# Revit family: xxxSoap_Dispenser-Grohe-Universal-40553_Series
name_source: partatom
category: Specialty Equipment
units: mm (PartAtom-declared; Revit-internal decimal feet)

## family parameters
Always vertical = No
Cut with Voids When Loaded = No
OmniClass Number = 23.40.20.21.34
OmniClass Title = Soap Holders, Dispensers
Part Type = Normal
Room Calculation Point = No
Round Connector Dimension = Use Diameter
Shared = Yes
Work Plane-Based = Yes

## types (2) — shared parameters
Assembly Code = C1030200
Capacity = 15 oz.
Compliance Certifications = Energy Policy Act of 1992, CSA B125.1 & ASME A112.18.1
Default Elevation = 0"
Description = Grohe Zedra Soap Dispenser
Diameter = 1 3/4"
Height = 3 3/16"
Installation Instruction Link = https://americanstandard.box.com
Length = 3"
Manufacturer = GROHE
Overall Length = 3 7/8"
Price = Prices may vary. Please consult Manufacturer Representative for most up-to-date price list.
Product Documentation Link = https://americanstandard.box.com
Product Page URL = https://www.grohe.us
Revised Date = 03/03/2022
URL = https://www.grohe.us

## per-type parameters (varying)
| type | Finish | Material |
| 40553000 | Brass-Grohe-000-StarLight Chrome | Brass-Grohe-000-StarLight Chrome |
| 40553DC0 | Brass-Grohe-DC0-SuperSteel Infinity Finish | Brass-Grohe-DC0-SuperSteel Infinity Finish |

note: column(s) folded — value = type name in every type: Model

## geometry (parser evidence)
native form markers: Sweep x2
no freeform markers — native parametric forms only
